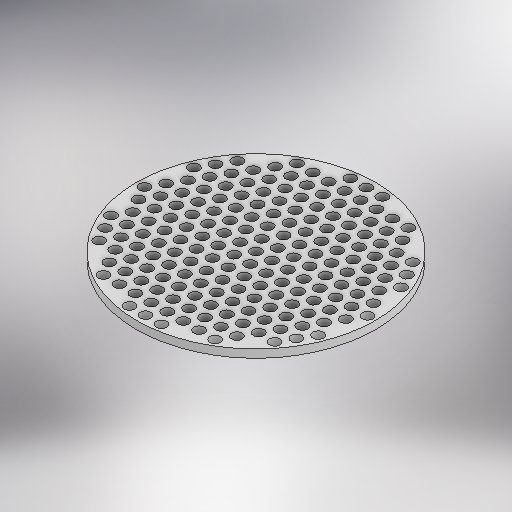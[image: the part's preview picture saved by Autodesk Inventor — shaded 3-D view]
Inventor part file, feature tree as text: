
AUTODESK INVENTOR PART (.ipt)
format: ipt  version: 2025 (Build 290162000, 162)  size: 684,032 bytes
history: native  units: mm
features: extrude x1, sketch x1
ambient origin geometry x8: Origin, YZ Plane, XZ Plane, XY Plane, X Axis, Y Axis, Z Axis, Center Point
bodies: Body1 (feature_tree)
feature tree (2):
  extrude  "拉伸2"  Depth=1.5mm
  sketch  "草图2"  dims[d27=2.0mm d28=2.0mm d29=2.0mm d30=2.0mm d31=2.0mm d32=2.0mm d33=2.0mm d34=2.0mm d35=2.0mm d36=2.0mm d37=2.0mm d38=2.0mm d39=2.0mm d42=2.0mm d44=2.0mm d45=2.0mm d46=2.0mm d47=2.0mm d48=2.0mm d49=2.0mm d50=2.0mm d51=2.0mm d55=2.0mm d56=2.0mm d57=2.0mm d58=2.0mm d59=2.0mm d60=2.0mm d61=2.0mm d62=2.0mm d63=2.0mm d64=2.0mm d65=2.0mm d66=2.0mm d67=2.0mm d68=2.0mm d69=2.0mm d70=2.0mm d71=2.0mm d72=2.0mm d73=2.0mm d74=2.0mm d75=2.0mm d76=2.0mm d77=2.0mm d78=2.0mm d79=2.0mm d82=2.0mm d83=2.0mm d84=2.0mm d85=2.0mm d86=2.0mm d87=2.0mm d89=2.0mm d91=2.0mm d92=2.0mm d94=2.0mm d95=2.0mm d96=2.0mm d97=2.0mm d98=2.0mm d99=2.0mm d100=2.0mm d101=2.0mm d102=2.0mm d103=2.0mm d104=2.0mm d105=2.0mm d106=2.0mm d107=2.0mm d109=2.0mm d110=2.0mm d111=2.0mm d113=2.0mm d114=2.0mm d116=2.0mm d117=2.0mm d118=2.0mm d119=2.0mm d120=2.0mm d121=2.0mm d122=2.0mm d123=2.0mm d124=2.0mm d125=2.0mm d126=2.0mm d127=2.0mm d128=2.0mm d129=2.0mm d130=2.0mm d131=2.0mm d132=2.0mm d133=2.0mm d134=2.0mm d135=2.0mm d136=2.0mm d137=2.0mm d138=2.0mm d139=2.0mm d140=2.0mm d141=2.0mm d142=45.0mm d143=1.5mm d144=0.0mm d3=0.5mm d4=0.872665mm d5=0.5mm d6=0.872665mm]
